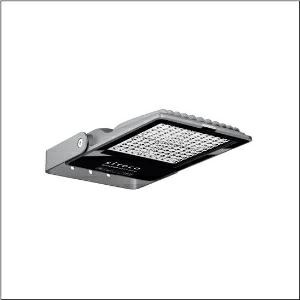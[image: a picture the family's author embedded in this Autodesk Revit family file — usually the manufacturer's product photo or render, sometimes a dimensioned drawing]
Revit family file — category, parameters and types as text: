
# Revit family: sicompact_r__31_mini___pl32_5xa7571b1k23_124a
name_source: partatom
category: Lighting Fixtures
units: mm (PartAtom-declared; Revit-internal decimal feet)

## family parameters
Cut with Voids When Loaded = No
Host = Face
Light Source = No
Part Type = Normal
Room Calculation Point = No
Round Connector Dimension = Use Diameter
Shared = No

## types (1)
- SiCompact® 31 mini  PL32 (1 x LED, 8000 lm, 48 W, 3000K)
    Apparent Load = 48 VA
    CIE Flux Codes = 32 69 98 100 100
    Color Rendering = 70
    Color Temperature = 3000K
    Default Elevation = 1800 mm
    Description = SiCompact® 31 mini, floodlight, primary light control with lens, of plastic, of toughened safety glass, transparent, light distribution: PL32, light emission: direct distribution, primary light characteristic: asymmetric, installation type: surface-mounted, LED, High Power LED, rated luminous flux: 8.000lm, luminous efficacy: 167lm/W, light colour: 730, colour temperature: 3000K, control gear: ECG, with cable, 3x 1.5mm², mains connection: 220..240V, AC, 50/60Hz, connection cable pre-assembled, cable length: 2m, rated input power: 48W, of diecast aluminium, specular, metallic grey (RAL 9006), length: 461mm, width: 261mm, height: 62mm, bracket, of sheet steel, coated, metallic grey (RAL 9006), ON/OFF, protection rating (complete): IP66, insulation class (complete): insulation class I (protective earthing), certification: CE, ENEC, impact resistance: IK08, permissible operating ambient temperature: -40..+45°C, packaging unit: 1 piece

Light Distribution: PL32
    Height = 62 mm  [stored 0.203412 ft]
    Lamp = 1 x LED
    Lamp Light Flux = 8000 lm
    Lamp Power = 48 W
    Lamp count = 1
    Length = 460 mm
    Luminous efficacy = 167 lm/W
    Manufacturer = Siteco
    ModVariant = No
    Model = 5XA7571B1K23
    Mounting Place = Wall
    Mounting Type = Surface mounted
    Number of Poles = 1
    OnlyDefault = Yes
    Power Factor = 1
    Product Name = SiCompact® 31 mini | PL32
    Product group = floodlight | wall mounted
    ProductGroupID = 2001
    Protection Class = Protection class I
    Protection Degree = IP 66
    RLX_Detail_Level = 1
    RLX_Emergency_Light_Flux = 0 lm
    RLX_Emergency_Type = 0
    RLX_Emergency_Type_DB = No
    RlxData = <blob elided: 126741 chars, md5=4a57b429>
    Socket = socket
    Standby Power = 0 W
    System Light Flux = 8000 lm
    System Power = 48 W
    Type Comments = Product without accessories
    Type Image = l_1006951.jpg
    URL = http://relux.com
    VarID = ---
    Voltage = 0 V
    Weight = 0.00 kg
    Width = 260 mm

note: [stored X ft] marks values corroborated as IEEE doubles in the binary element streams (Revit-internal decimal feet)

## geometry (parser evidence)
native form markers: Blend x4, Sweep x12
no freeform markers — native parametric forms only
